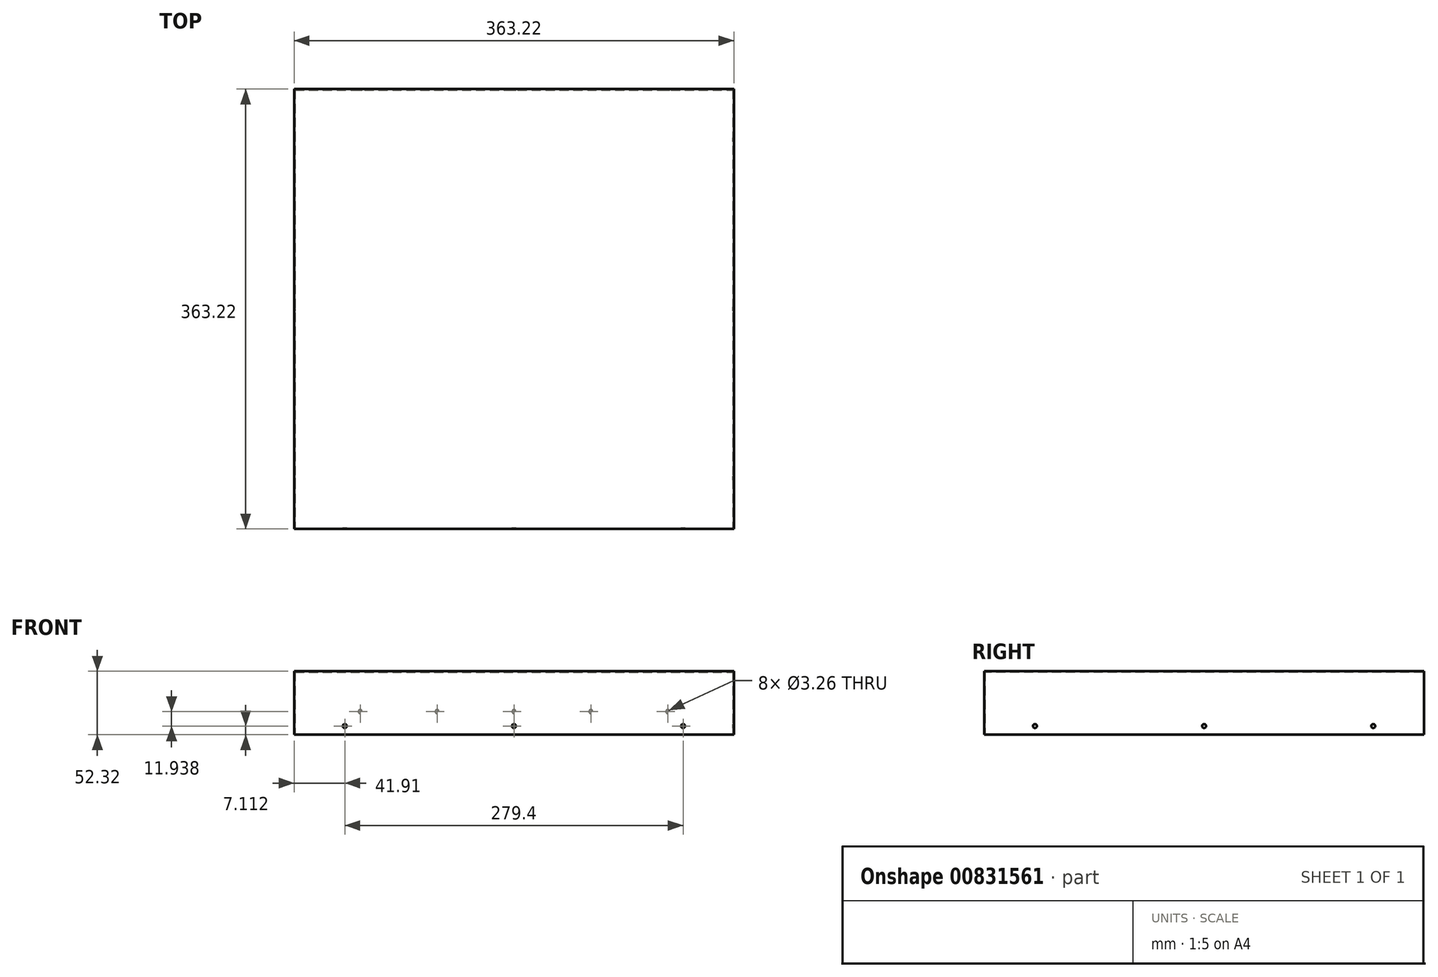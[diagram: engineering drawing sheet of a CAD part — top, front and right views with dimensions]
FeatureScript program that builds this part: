
annotation { "Feature Type Name" : "Feature", "Feature Type Description" : "" }
export const myFeature = defineFeature(function(context is Context, id is Id, definition is map)
    precondition{}
    {
        {
            var Q0;
            Q0=qCreatedBy(makeId("Top.planeOp"),FACE);
            var sketch = newSketch(context, id + "F0", { "sketchPlane" : qUnion([Q0])});
            skLineSegment(sketch, "E0.bottom", {"start": v(-181.61, 181.61) * mm, "end": v(181.6, 181.61) * mm});
            skLineSegment(sketch, "E0.top", {"start": v(-181.61, -181.61) * mm, "end": v(181.61, -181.61) * mm});
            skLineSegment(sketch, "E0.left", {"start": v(-181.61, 181.61) * mm, "end": v(-181.61, -181.61) * mm});
            skLineSegment(sketch, "E0.right", {"start": v(181.6, 181.61) * mm, "end": v(181.61, -181.6) * mm});
            skLineSegment(sketch, "E1", {"start": v(0, 181.61) * mm, "end": v(0, 0) * mm});
            skLineSegment(sketch, "E2", {"start": v(0, 0) * mm, "end": v(0, -181.61) * mm});
            skSolve(sketch);
        }
        {
            var Q0;
            Q0=qSketchRegion(id+"F0",true);
            extrude(context, id + "F1", {"entities" : qUnion([Q0]), "depth" : 52.32 * mm, "offsetDistance" : 25.4 * mm});
        }
        {
            var Q0;
            Q0=makeQuery(id+"F1.opExtrude","CAP_FACE",FACE,{"disambiguationData":[OSD([sQuery(id+"F0.wireOp",EDGE,"E0.bottom"),sQuery(id+"F0.wireOp",EDGE,"E0.top"),sQuery(id+"F0.wireOp",EDGE,"E0.left"),sQuery(id+"F0.wireOp",EDGE,"E0.right"),sQuery(id+"F0.wireOp",EDGE,"fc65cf4e-397e-4326-95eb-a6be6ae45aa2.filletArc"),sQuery(id+"F0.wireOp",EDGE,"f2cdcc59-0d75-48d6-b18f-6f8fbd6c8b9e.filletArc"),sQuery(id+"F0.wireOp",EDGE,"7446712d-ec4b-40db-8b68-e0c5e1381eb3.filletArc"),sQuery(id+"F0.wireOp",EDGE,"67f8c840-68b2-45fe-9efc-351ec261f702.filletArc")])],"isStart":true});
            shell(context, id + "F2", {"entities" : qUnion([Q0]), "thickness" : 0.76 * mm});
        }
        {
            var Q0;
            Q0=makeQuery(id+"F1.opExtrude","SWEPT_FACE",FACE,{"disambiguationData":[OSD([sQuery(id+"F0.wireOp",EDGE,"E0.top")])]});
            var sketch = newSketch(context, id + "F3", { "sketchPlane" : qUnion([Q0])});
            skPoint(sketch, "E3", {"position": v(-139.7, 7.11) * mm});
            skPoint(sketch, "E4", {"position": v(0, 7.11) * mm});
            skPoint(sketch, "E5", {"position": v(139.7, 7.11) * mm});
            skLineSegment(sketch, "E6", {"start": v(-139.7, 7.11) * mm, "end": v(0, 7.11) * mm});
            skLineSegment(sketch, "E7", {"start": v(0, 7.11) * mm, "end": v(139.7, 7.11) * mm});
            skLineSegment(sketch, "E8", {"start": v(0, 0) * mm, "end": v(0, 7.11) * mm});
            skSolve(sketch);
        }
        {
            var Q0;
            Q0=sQuery(id+"F3.wireOp",VERTEX,"E3");
            var Q1;
            Q1=sQuery(id+"F3.wireOp",VERTEX,"E4");
            var Q2;
            Q2=sQuery(id+"F3.wireOp",VERTEX,"E5");
            var Q3;
            Q3=makeQuery(id+"F1.opExtrude","SWEPT_BODY",BODY,{"disambiguationData":[OSD([sQuery(id+"F0.wireOp",EDGE,"E0.bottom"),sQuery(id+"F0.wireOp",EDGE,"E0.top"),sQuery(id+"F0.wireOp",EDGE,"E0.left"),sQuery(id+"F0.wireOp",EDGE,"E0.right"),sQuery(id+"F0.wireOp",EDGE,"fc65cf4e-397e-4326-95eb-a6be6ae45aa2.filletArc"),sQuery(id+"F0.wireOp",EDGE,"f2cdcc59-0d75-48d6-b18f-6f8fbd6c8b9e.filletArc"),sQuery(id+"F0.wireOp",EDGE,"7446712d-ec4b-40db-8b68-e0c5e1381eb3.filletArc"),sQuery(id+"F0.wireOp",EDGE,"67f8c840-68b2-45fe-9efc-351ec261f702.filletArc")])]});
            hole(context, id + "F4", {"style" : HoleStyle.SIMPLE, "endStyle" : HoleEndStyle.BLIND, "standardTappedOrClearance" : lookupTablePath({ "standard" : "ANSI", "size" : "#30 (0.13)", "type" : "Drilled" }), "standardBlindInLast" : lookupTablePath({ "standard" : "ANSI", "size" : "#30", "type" : "Drilled" }), "holeDiameter" : 3.26 * mm, "majorDiameter" : 6.35 * mm, "holeDepth" : 0.76 * mm, "isTappedThrough" : true, "tappedDepth" : 12.7 * mm, "tapClearance" : 3, "locations" : qUnion([Q0, Q1, Q2]), "scope" : qUnion([Q3])});
        }
        {
            var Q0;
            Q0=makeQuery(id+"F1.opExtrude","SWEPT_FACE",FACE,{"disambiguationData":[OSD([sQuery(id+"F0.wireOp",EDGE,"E0.left")])]});
            var sketch = newSketch(context, id + "F5", { "sketchPlane" : qUnion([Q0])});
            skPoint(sketch, "E9", {"position": v(0, 7.11) * mm});
            skPoint(sketch, "E10", {"position": v(-139.7, 7.11) * mm});
            skPoint(sketch, "E11", {"position": v(139.7, 7.11) * mm});
            skLineSegment(sketch, "E12", {"start": v(-139.7, 7.11) * mm, "end": v(0, 7.11) * mm});
            skLineSegment(sketch, "E13", {"start": v(139.7, 7.11) * mm, "end": v(0, 7.11) * mm});
            skLineSegment(sketch, "E14", {"start": v(0, 7.11) * mm, "end": v(0, 0) * mm});
            skSolve(sketch);
        }
        {
            var Q0;
            Q0=sQuery(id+"F5.wireOp",VERTEX,"E10");
            var Q1;
            Q1=sQuery(id+"F5.wireOp",VERTEX,"E9");
            var Q2;
            Q2=sQuery(id+"F5.wireOp",VERTEX,"E11");
            var Q3;
            Q3=makeQuery(id+"F1.opExtrude","SWEPT_BODY",BODY,{"disambiguationData":[OSD([sQuery(id+"F0.wireOp",EDGE,"E0.bottom"),sQuery(id+"F0.wireOp",EDGE,"E0.top"),sQuery(id+"F0.wireOp",EDGE,"E0.left"),sQuery(id+"F0.wireOp",EDGE,"E0.right"),sQuery(id+"F0.wireOp",EDGE,"fc65cf4e-397e-4326-95eb-a6be6ae45aa2.filletArc"),sQuery(id+"F0.wireOp",EDGE,"f2cdcc59-0d75-48d6-b18f-6f8fbd6c8b9e.filletArc"),sQuery(id+"F0.wireOp",EDGE,"7446712d-ec4b-40db-8b68-e0c5e1381eb3.filletArc"),sQuery(id+"F0.wireOp",EDGE,"67f8c840-68b2-45fe-9efc-351ec261f702.filletArc")])]});
            hole(context, id + "F6", {"style" : HoleStyle.SIMPLE, "endStyle" : HoleEndStyle.THROUGH, "standardTappedOrClearance" : lookupTablePath({ "standard" : "ANSI", "size" : "#30 (0.13)", "type" : "Drilled" }), "standardBlindInLast" : lookupTablePath({ "standard" : "ANSI", "size" : "#30", "type" : "Drilled" }), "holeDiameter" : 3.26 * mm, "majorDiameter" : 6.35 * mm, "isTappedThrough" : true, "tappedDepth" : 12.7 * mm, "tapClearance" : 3, "locations" : qUnion([Q0, Q1, Q2]), "scope" : qUnion([Q3])});
        }
        {
            var Q0;
            Q0=makeQuery(id+"F1.opExtrude","SWEPT_FACE",FACE,{"disambiguationData":[OSD([sQuery(id+"F0.wireOp",EDGE,"E0.bottom")])]});
            var sketch = newSketch(context, id + "F7", { "sketchPlane" : qUnion([Q0])});
            skPoint(sketch, "E15", {"position": v(-127, 19.05) * mm});
            skPoint(sketch, "E16", {"position": v(-63.5, 19.05) * mm});
            skPoint(sketch, "E17", {"position": v(0, 19.05) * mm});
            skPoint(sketch, "E18", {"position": v(63.5, 19.05) * mm});
            skPoint(sketch, "E19", {"position": v(127, 19.05) * mm});
            skLineSegment(sketch, "E20", {"start": v(-127, 19.05) * mm, "end": v(-63.5, 19.05) * mm});
            skLineSegment(sketch, "E21", {"start": v(-63.5, 19.05) * mm, "end": v(0, 19.05) * mm});
            skLineSegment(sketch, "E22", {"start": v(0, 19.05) * mm, "end": v(63.5, 19.05) * mm});
            skLineSegment(sketch, "E23", {"start": v(63.5, 19.05) * mm, "end": v(127, 19.05) * mm});
            skLineSegment(sketch, "E24", {"start": v(0, 19.05) * mm, "end": v(0, 52.32) * mm});
            skSolve(sketch);
        }
        {
            var Q0;
            Q0=sQuery(id+"F7.wireOp",VERTEX,"E15");
            var Q1;
            Q1=sQuery(id+"F7.wireOp",VERTEX,"E16");
            var Q2;
            Q2=sQuery(id+"F7.wireOp",VERTEX,"E17");
            var Q3;
            Q3=sQuery(id+"F7.wireOp",VERTEX,"E18");
            var Q4;
            Q4=sQuery(id+"F7.wireOp",VERTEX,"E19");
            var Q5;
            Q5=makeQuery(id+"F1.opExtrude","SWEPT_BODY",BODY,{"disambiguationData":[OSD([sQuery(id+"F0.wireOp",EDGE,"E0.bottom"),sQuery(id+"F0.wireOp",EDGE,"E0.top"),sQuery(id+"F0.wireOp",EDGE,"E0.left"),sQuery(id+"F0.wireOp",EDGE,"E0.right")])]});
            hole(context, id + "F8", {"style" : HoleStyle.SIMPLE, "endStyle" : HoleEndStyle.BLIND, "standardTappedOrClearance" : lookupTablePath({ "standard" : "ANSI", "size" : "#30 (0.13)", "type" : "Drilled" }), "standardBlindInLast" : lookupTablePath({ "standard" : "ANSI", "size" : "#30", "type" : "Drilled" }), "holeDiameter" : 3.26 * mm, "majorDiameter" : 6.35 * mm, "holeDepth" : 0.76 * mm, "isTappedThrough" : true, "tappedDepth" : 12.7 * mm, "tapClearance" : 3, "locations" : qUnion([Q0, Q1, Q2, Q3, Q4]), "scope" : qUnion([Q5])});
        }
    });
